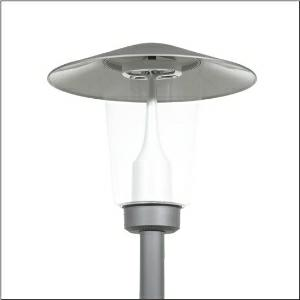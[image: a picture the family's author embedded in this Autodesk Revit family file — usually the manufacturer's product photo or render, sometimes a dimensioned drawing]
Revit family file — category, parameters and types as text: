
# Revit family: pilzleuchte_iq___st1_2a_5xa5235ef14h_b780
name_source: partatom
category: Lighting Fixtures
units: mm (PartAtom-declared; Revit-internal decimal feet)

## family parameters
Cut with Voids When Loaded = No
Host = Face
Light Source = No
Part Type = Normal
Room Calculation Point = No
Round Connector Dimension = Use Diameter
Shared = No

## types (1)
- --- (1 x LED, 1550 lm, 10.5 W, 3000K)
    Apparent Load = 11 VA
    CIE Flux Codes = 24 61 93 98 100
    Color Rendering = 70
    Color Temperature = 3000K
    Default Elevation = 1800 mm
    Description = Mushroom Luminaire iQ, mast luminaire, Module 540 iQ-SR, primary light control with 3 zone facetted reflector, of plastic, silver coated, highly specular, structured, primary optical cover: cover, of PMMA, transparent, light distribution: ST1.2a, light emission: direct distribution, primary light characteristic: asymmetric, installation type: post-top, LED, High Power LED, rated luminous flux: 1.550lm, luminous efficacy: 148lm/W, light colour: 730, colour temperature: 3000K, control gear: iQ Street-Remote, control: Auto-Match, Temp-Guard, Lumen-Switch, Night-Set, Smart-Wire, Light-Fading, Desk-Remote (wireless, voltage-free reading and setting of iQ features in the workshop via application-optimized NFC function/RFID function), optimised constant luminous flux control (CLO 2.0), Street-Remote, pre-setting: logarithmic dimming characteristic, with terminal, 6-pole, max. 2.5mm², mains connection: 230..240V, AC, 50/60Hz, start of lifetime: 11W, end of service life: 11W, reduction: 5W, luminaire housing, upper part, of glass-fibre reinforced polyester, coated, Siteco® metallic grey (DB 702S), diameter: 650mm, height: 586mm, spigot size: d x l = 76 x 70mm (post-top) | with reducer (optional accessory) 60 x 70mm, mounting height: 3..5m, post-top mast mounting element, of diecast aluminium, coated, Siteco® metallic grey (DB 702S), Module 540 iQ-SR, traffic white (RAL 9016), equipment: standard, protection rating (complete): IP65, insulation class (complete): insulation class II (safety insulation), certification: CE, ENEC, VDE, packaging unit: 1 piece

Light Distribution: ST1.2a
    Height = 586 mm
    Lamp = 1 x LED
    Lamp Light Flux = 1550 lm
    Lamp Power = 10.5 W
    Lamp count = 1
    Length = 650 mm
    Luminous efficacy = 148 lm/W
    Manufacturer = Siteco
    ModVariant = No
    Model = 5XA5235EF14H
    Number of Poles = 1
    OnlyDefault = Yes
    Power Factor = 1
    Product Name = Pilzleuchte iQ | ST1.2a
    Product group = mast luminaire | pylon top
    ProductGroupID = 6100
    Protection Class = Protection class II
    Protection Degree = IP 65
    RLX_Detail_Level = 1
    RLX_Emergency_Light_Flux = 0 lm
    RLX_Emergency_Type = 0
    RLX_Emergency_Type_DB = No
    RlxData = <blob elided: 123085 chars, md5=fe834067>
    Socket = socket
    Standby Power = 0 W
    System Light Flux = 1550 lm
    System Power = 11 W
    Type Comments = factory setting: luminous flux: 100 % | dim-lin: 254 | 419 mA
    Type Image = l_1006077.jpg
    URL = http://relux.com
    VarID = @adj_160790
    Voltage = 0 V
    Weight = 0.00 kg
    Width = 0 mm  [stored 0 ft]

note: [stored X ft] marks values corroborated as IEEE doubles in the binary element streams (Revit-internal decimal feet)

## geometry (parser evidence)
native form markers: Blend x4, Sweep x12
no freeform markers — native parametric forms only
